# Revit family: P24038A75FTT-B.V3 L-R
name_source: partatom
category: Plumbing Fixtures
units: mm (PartAtom-declared; Revit-internal decimal feet)

## family parameters
Always vertical = Yes
Cut with Voids When Loaded = No
OmniClass Number = 23.45.05.14.17
OmniClass Title = Showers
Part Type = Normal
Room Calculation Point = No
Round Connector Dimension = Use Diameter
Shared = No
Work Plane-Based = No

## types (4) — shared parameters
Assembly Code = D2010710
Keynote = 22 40 00.B3
Manufacturer = Best Bath Systems, Inc.
Type Comments = ADA Compliant
URL = http://www.bestbath.com
Unit Depth = 38 1/4"
Unit Width = 38 1/2"

## per-type parameters (varying)
| type | Description | Threshold Height | Unit Height |
| P24038A75FTB.V3 | Trench Drain Pan, Bevelled Threshold | 3/4" | 5 3/4" |
| P24038A75FTT.V3 | Trench Drain Pan, Traditional Bullnose Threshold | 3/4" | 5 3/4" |
| P24038A2FTT.V3 | Trench Drain Pan, Traditional Bullnose Threshold | 2" | 7" |
| P24038A2FTB.V3 | Trench Drain Pan, Bevelled Threshold | 2" | 7" |

note: column(s) folded — value = type name in every type: Model

## geometry (parser evidence)
native form markers: Blend x8, Sweep x1
no freeform markers — native parametric forms only
